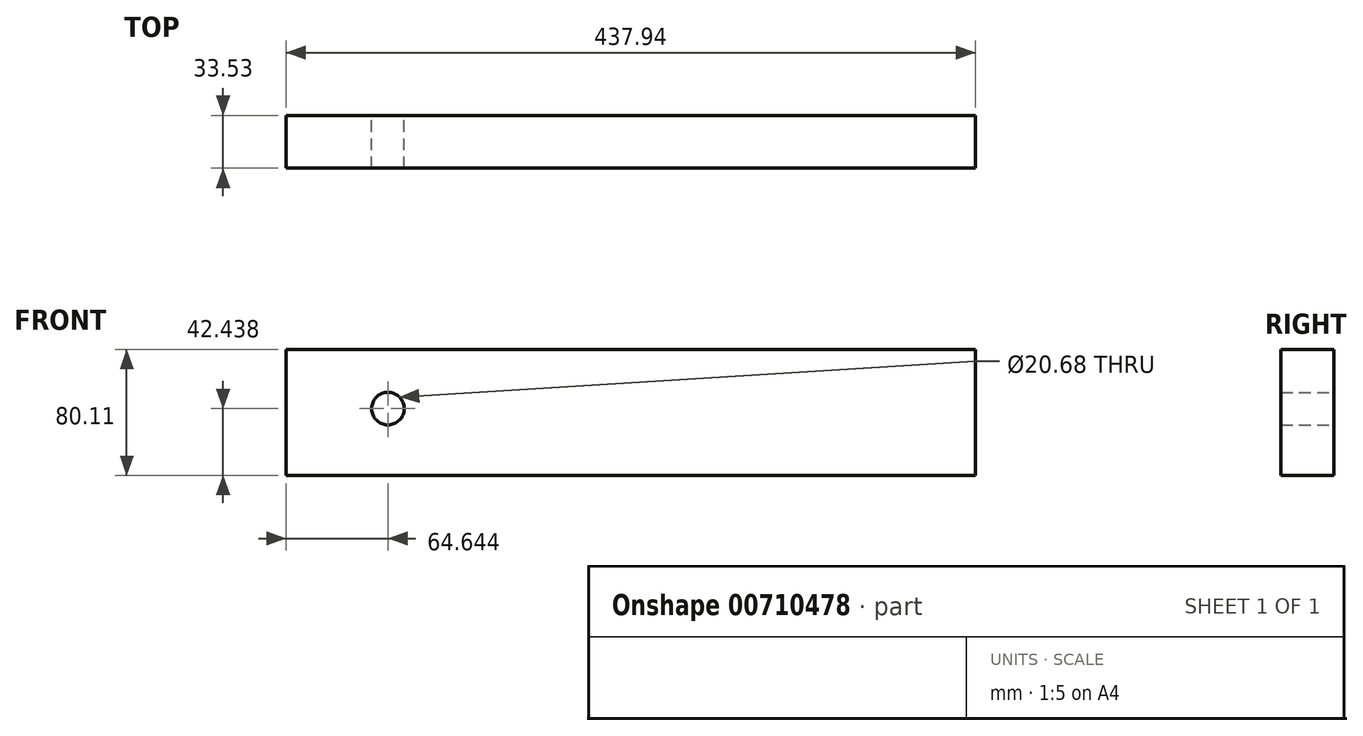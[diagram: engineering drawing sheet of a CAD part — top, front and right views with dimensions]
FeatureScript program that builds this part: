
annotation { "Feature Type Name" : "Feature", "Feature Type Description" : "" }
export const myFeature = defineFeature(function(context is Context, id is Id, definition is map)
    precondition{}
    {
        {
            var Q0;
            Q0=qCreatedBy(makeId("Front.planeOp"),FACE);
            var sketch = newSketch(context, id + "F0", { "sketchPlane" : qUnion([Q0])});
            skLineSegment(sketch, "E0.bottom", {"start": v(-57, 41.44) * mm, "end": v(380.93, 41.44) * mm});
            skLineSegment(sketch, "E0.top", {"start": v(-57, -38.67) * mm, "end": v(380.93, -38.67) * mm});
            skLineSegment(sketch, "E0.left", {"start": v(-57, 41.44) * mm, "end": v(-57, -38.67) * mm});
            skLineSegment(sketch, "E0.right", {"start": v(380.93, 41.44) * mm, "end": v(380.93, -38.67) * mm});
            skCircle(sketch, "E1", {"center": v(7.63, 3.77) * mm, "radius": 10.34 * mm});
            skSolve(sketch);
        }
        {
            var Q0;
            Q0=makeQuery(id+"F0.imprint","IMPRINT",FACE,{"disambiguationData":[TD([[makeQuery(id+"F0.imprint","IMPRINT",EDGE,{"derivedFrom":sQuery(id+"F0.wireOp",EDGE,"E0.bottom")}),-1.0]])]});
            extrude(context, id + "F1", {"entities" : qUnion([Q0]), "depth" : 33.53 * mm, "offsetDistance" : 25.4 * mm});
        }
    });
